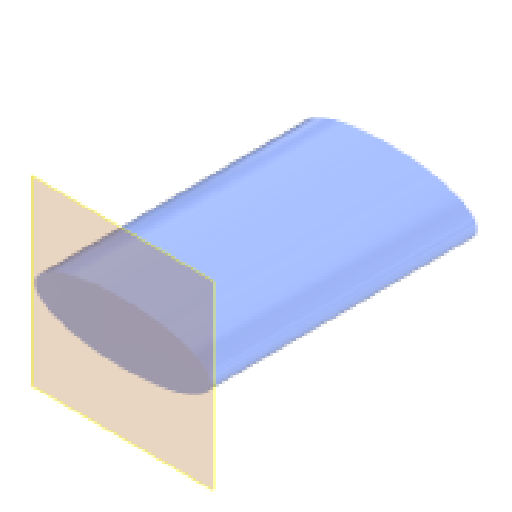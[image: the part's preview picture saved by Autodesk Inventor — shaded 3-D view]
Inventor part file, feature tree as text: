
AUTODESK INVENTOR PART (.ipt)
format: ipt  version: 2023 (Build 270158000, 158)  size: 94,208 bytes
history: native  units: in
note: dims shown in document units (in); Inventor stores cm internally (conversion verified against a paired STEP export)
features: other x3, sketch x2, plane x1, extrude x1
ambient origin geometry x8: Origin, YZ Plane, XZ Plane, XY Plane, X Axis, Y Axis, Z Axis, Center Point
bodies: Solid1 (feature_tree)
feature tree (7):
  plane  "Work Plane1"
  extrude  "Extrusion1"  [1 undecoded]
  sketch  "Sketch3"
  sketch  "Sketch1"  dims[d0=118.1102in d1=0.0in]
  other  "<userpath>\vaRLnt\v3\demo\sigmaPoint\Assembly1.iam"
  other  "Assembly1.iam"
  other  "column:1"
note: 1 required parameter value undecoded (feature->parameter linkage not recoverable at this tier; creation-order binding heuristic only, values carry confidence <= 0.55)
